# Revit family: Sanitary_Toilets_Sanindusa_New-WC-Care-F-D-Low-Level-Toilet
name_source: partatom
category: Plumbing Fixtures
revit_build: Autodesk Revit 2018 (Build: 20170223_1515(x64)
units: mm (PartAtom-declared; Revit-internal decimal feet)

## family parameters
Always vertical = Yes
Cut with Voids When Loaded = No
Host = Wall
OmniClass Number = 23.45.00.00
OmniClass Title = Sanitary, Laundry, and Cleaning Equipment
Part Type = Normal
Room Calculation Point = No
Round Connector Dimension = Use Diameter
Shared = No

## types (1)
- SanitaSimplesNewWccareDc129011004
    AssetType = Fixed
    CodePerformance = EN 997:2012 CL 1 - 7 A
    Color = White
    Constituents = Compatible toilet seats (not included): 2296100-New Wccare toilet seat and cover with slowclose system, 2295100-New Wccare toilet seat and cover, 2293100-New Wccare toilet seat and cover with frontal openning, 2291100-New Wccare toilet seat with cover and frontal openning with slowclose system, 2291100A-New wccare seat with frontal oppening, 2295100A-New wccare seat. Compatible water supply sistems (not inluded): 40133-Switch built-in cistern for low level wc with double flush, 445-Quadro built-in cistern for low level wc with double flush, 40433-Wallfit built-in cistern for low level wc with double flush, 5192941-Eco 3/4" exterior flush valve with horizontal medical lever, 5194941-Eco 3/4" built-in flush valve with horizontal medical lever, 5192941-Eco 3/4" exterior flush valve with horizontal medical lever.
    Cost = 0 $
    Description = F|D low level toilet for disabled
    DrainSize = 90 mm  [stored 0.295276 ft]
    Edition number = 1
    Features = Specific product for people with limited mobility or disabled.
    Finish = gloss
    InletDiameter = 50 mm
    InstallationDate = 1900-12-31T23:59:59
    Manufacturer = Sanindusa
    ManufacturerName = Sanindusa
    ManufacturerURL = www.tec.sanindusa.pt
    Material = Vitreous China
    ModelNumber = 129011004
    ModelReference = New Wccare
    Name = F|D low level toilet new wccare
    NominalHeight = 440 mm
    NominalLength = 380 mm
    NominalWidth = 575 mm
    Product Guid = 52976cc0-cf46-4ec7-8f5e-e80982ebd77e
    Product data url = https://bimobject.com
    ProductInformation = https://www.tec.sanindusa.pt
    ProductionYear = 2017
    Size = 380x575x440 mm
    SustainabilityPerformance = n/a
n/a
    URL = www.tec.sanindusa.pt
    Uniclass2015Code = Pr_40_20_93_78
    Uniclass2015Title = WC pans
    Uniclass2015Version = Products v1.6
    Version = 2
    WarrantyDescription = https://www.tec.sanindusa.pt
The warranty will come into force from the moment the warranty detachable bulletin that accompanies the product is received at Sanindusa or from the moment the product is sold to the distributer
Only if the customer issues a writen and justified (Country laws, state laws, commercial strategy) request to Sanindusa, may the above mentioned warranties be the object of a possible change.
The warranty will come into force from the moment the warranty detachable bulletin that accompanies the product is received at Sanindusa or from the moment the product is sold to the distributer.
Only if the customer issues a writen and justified (Country laws, state laws, commercial strategy) request to Sanindusa, may the above mentioned warranties be the object of a possible change. 2 Year warranty for electronic components.
    WarrantyDurationParts = 5
    WarrantyDurationUnit = year
    WarrantyStartDate = 1900-12-31T23:59:59
    Weight = 30.90 kg

note: [stored X ft] marks values corroborated as IEEE doubles in the binary element streams (Revit-internal decimal feet)

## geometry (parser evidence)
native form markers: Sweep x8
no freeform markers — native parametric forms only
